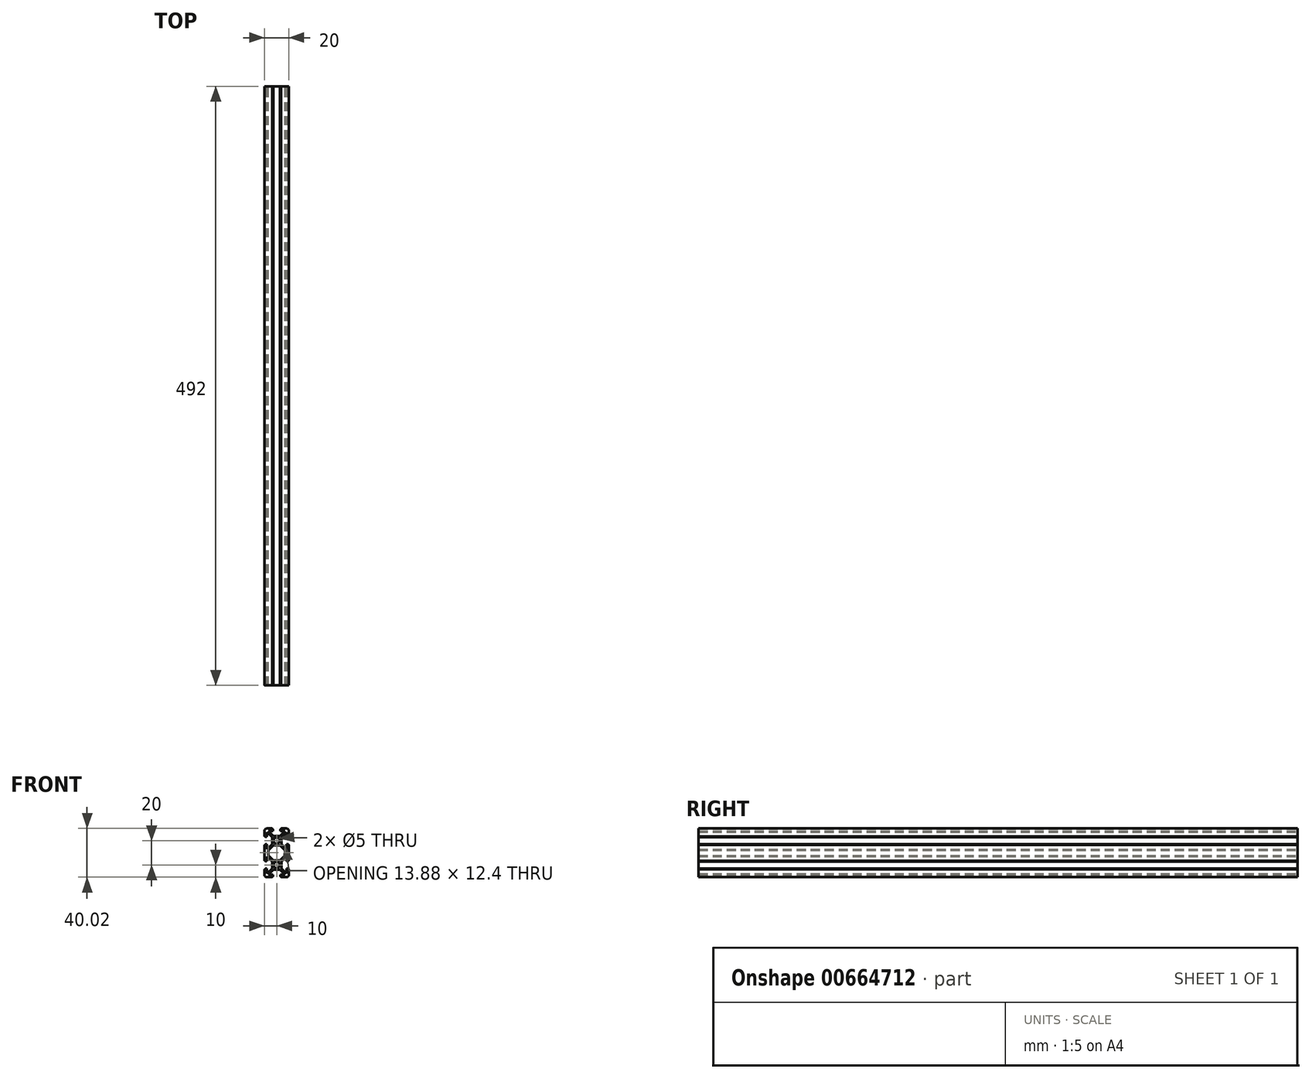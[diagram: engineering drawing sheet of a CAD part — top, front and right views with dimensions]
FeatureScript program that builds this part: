
annotation { "Feature Type Name" : "Feature", "Feature Type Description" : "" }
export const myFeature = defineFeature(function(context is Context, id is Id, definition is map)
    precondition{}
    {
        {
            var Q0;
            Q0=qCreatedBy(makeId("Front.planeOp"),FACE);
            var sketch = newSketch(context, id + "F0", { "sketchPlane" : qUnion([Q0])});
            skPoint(sketch, "E0.middle", {"position": v(10, -10) * mm});
            skPoint(sketch, "E1.visualSharp", {"position": v(0, 0) * mm});
            skArc(sketch, "E1.filletArc", {"start": v(2, 0) * mm, "mid": v(0.59, -0.59) * mm, "end": v(0, -2) * mm});
            skPoint(sketch, "E2.visualSharp", {"position": v(20, 0) * mm});
            skArc(sketch, "E2.filletArc", {"start": v(20, -2) * mm, "mid": v(19.41, -0.59) * mm, "end": v(18, 0) * mm});
            skPoint(sketch, "E3.visualSharp", {"position": v(20, -20) * mm});
            skLineSegment(sketch, "E4", {"start": v(2, 0) * mm, "end": v(6.5, 0) * mm});
            skLineSegment(sketch, "E5", {"start": v(6.5, 0) * mm, "end": v(6.5, -0.5) * mm});
            skLineSegment(sketch, "E6", {"start": v(13.02, -0.5) * mm, "end": v(13.5, -0.5) * mm});
            skLineSegment(sketch, "E7", {"start": v(13.5, 0.02) * mm, "end": v(18, 0) * mm});
            skLineSegment(sketch, "E8", {"start": v(20, -2) * mm, "end": v(20, -6.5) * mm});
            skLineSegment(sketch, "E9", {"start": v(20, -6.5) * mm, "end": v(19.5, -6.5) * mm});
            skLineSegment(sketch, "E10", {"start": v(19.5, -6.5) * mm, "end": v(19.5, -7) * mm});
            skLineSegment(sketch, "E11", {"start": v(13.83, -7.25) * mm, "end": v(13.83, -12.77) * mm});
            skLineSegment(sketch, "E12", {"start": v(19.53, -12.98) * mm, "end": v(19.54, -13.46) * mm});
            skLineSegment(sketch, "E13", {"start": v(12.74, -13.8) * mm, "end": v(7.26, -13.8) * mm});
            skLineSegment(sketch, "E14", {"start": v(6.2, -12.74) * mm, "end": v(6.2, -7.26) * mm});
            skLineSegment(sketch, "E15", {"start": v(0, -6.49) * mm, "end": v(0, -2) * mm});
            skLineSegment(sketch, "E16", {"start": v(7, -0.5) * mm, "end": v(7, -2) * mm});
            skLineSegment(sketch, "E17", {"start": v(7, -2) * mm, "end": v(3.06, -2) * mm});
            skLineSegment(sketch, "E18", {"start": v(3.06, -2) * mm, "end": v(7.26, -6.2) * mm});
            skLineSegment(sketch, "E19", {"start": v(12.74, -6.2) * mm, "end": v(16.94, -2) * mm});
            skLineSegment(sketch, "E20", {"start": v(16.94, -2) * mm, "end": v(13.02, -2) * mm});
            skLineSegment(sketch, "E21", {"start": v(19.53, -12.98) * mm, "end": v(18, -12.98) * mm});
            skLineSegment(sketch, "E22", {"start": v(18, -12.98) * mm, "end": v(18, -16.94) * mm});
            skLineSegment(sketch, "E23", {"start": v(18, -16.94) * mm, "end": v(13.83, -12.77) * mm});
            skLineSegment(sketch, "E24", {"start": v(13.83, -7.25) * mm, "end": v(18, -3.06) * mm});
            skLineSegment(sketch, "E25", {"start": v(18, -3.06) * mm, "end": v(18, -7) * mm});
            skLineSegment(sketch, "E26", {"start": v(18, -7) * mm, "end": v(19.5, -7) * mm});
            skLineSegment(sketch, "E27", {"start": v(16.94, -18) * mm, "end": v(12.74, -13.8) * mm});
            skLineSegment(sketch, "E28", {"start": v(7.26, -13.8) * mm, "end": v(3.06, -18) * mm});
            skLineSegment(sketch, "E29", {"start": v(0.5, -6.49) * mm, "end": v(0.5, -7) * mm});
            skLineSegment(sketch, "E30", {"start": v(0.5, -7) * mm, "end": v(2, -7) * mm});
            skLineSegment(sketch, "E31", {"start": v(2, -7) * mm, "end": v(2, -3.08) * mm});
            skLineSegment(sketch, "E32", {"start": v(2, -3.08) * mm, "end": v(6.2, -7.26) * mm});
            skLineSegment(sketch, "E33", {"start": v(6.2, -12.74) * mm, "end": v(2, -16.94) * mm});
            skLineSegment(sketch, "E34", {"start": v(2, -16.94) * mm, "end": v(2, -13) * mm});
            skLineSegment(sketch, "E35", {"start": v(2, -13) * mm, "end": v(0.5, -13) * mm});
            skLineSegment(sketch, "E36", {"start": v(0.5, -13) * mm, "end": v(0.5, -13.5) * mm});
            skLineSegment(sketch, "E37", {"start": v(0.5, -13.5) * mm, "end": v(0, -13.5) * mm});
            skCircle(sketch, "E38", {"center": v(10, -10) * mm, "radius": 2.5 * mm});
            skLineSegment(sketch, "E39", {"start": v(13.5, 0.02) * mm, "end": v(13.5, -0.5) * mm});
            skLineSegment(sketch, "E40", {"start": v(6.5, -0.5) * mm, "end": v(7, -0.5) * mm});
            skLineSegment(sketch, "E41", {"start": v(13.02, -0.5) * mm, "end": v(13.02, -2) * mm});
            skLineSegment(sketch, "E42", {"start": v(7.26, -6.2) * mm, "end": v(12.74, -6.2) * mm});
            skLineSegment(sketch, "E43", {"start": v(0, -6.49) * mm, "end": v(0.5, -6.49) * mm});
            skLineSegment(sketch, "E44", {"start": v(19.54, -13.46) * mm, "end": v(20, -13.46) * mm});
            skPoint(sketch, "E45.middle", {"position": v(10, -30) * mm});
            skPoint(sketch, "E46.visualSharp", {"position": v(0, -20) * mm});
            skPoint(sketch, "E47.visualSharp", {"position": v(20, -40) * mm});
            skArc(sketch, "E47.filletArc", {"start": v(18, -40) * mm, "mid": v(19.41, -39.41) * mm, "end": v(20, -38) * mm});
            skArc(sketch, "E48.filletArc", {"start": v(0, -38) * mm, "mid": v(0.59, -39.41) * mm, "end": v(2, -40) * mm});
            skLineSegment(sketch, "E49", {"start": v(20, -26.5) * mm, "end": v(19.5, -26.5) * mm});
            skLineSegment(sketch, "E50", {"start": v(19.5, -26.5) * mm, "end": v(19.5, -27) * mm});
            skLineSegment(sketch, "E51", {"start": v(13.83, -27.25) * mm, "end": v(13.83, -32.77) * mm});
            skLineSegment(sketch, "E52", {"start": v(19.53, -32.98) * mm, "end": v(19.54, -33.46) * mm});
            skLineSegment(sketch, "E53", {"start": v(20, -33.46) * mm, "end": v(20, -38) * mm});
            skLineSegment(sketch, "E54", {"start": v(18, -40) * mm, "end": v(13.5, -40) * mm});
            skLineSegment(sketch, "E55", {"start": v(13.5, -40) * mm, "end": v(13.5, -39.5) * mm});
            skLineSegment(sketch, "E56", {"start": v(12.74, -33.8) * mm, "end": v(7.26, -33.8) * mm});
            skLineSegment(sketch, "E57", {"start": v(7, -39.5) * mm, "end": v(6.5, -39.5) * mm});
            skLineSegment(sketch, "E58", {"start": v(6.5, -39.5) * mm, "end": v(6.5, -40) * mm});
            skLineSegment(sketch, "E59", {"start": v(6.5, -40) * mm, "end": v(2, -40) * mm});
            skLineSegment(sketch, "E60", {"start": v(0, -38) * mm, "end": v(0, -33.5) * mm});
            skLineSegment(sketch, "E61", {"start": v(6.2, -32.74) * mm, "end": v(6.2, -27.26) * mm});
            skLineSegment(sketch, "E62", {"start": v(7, -39.5) * mm, "end": v(7, -38) * mm});
            skLineSegment(sketch, "E63", {"start": v(13.02, -39.5) * mm, "end": v(13.02, -38) * mm});
            skLineSegment(sketch, "E64", {"start": v(13.02, -38) * mm, "end": v(16.94, -38) * mm});
            skLineSegment(sketch, "E65", {"start": v(3.06, -22) * mm, "end": v(7.26, -26.2) * mm});
            skLineSegment(sketch, "E66", {"start": v(12.74, -26.2) * mm, "end": v(16.94, -22) * mm});
            skLineSegment(sketch, "E67", {"start": v(19.53, -32.98) * mm, "end": v(18, -32.98) * mm});
            skLineSegment(sketch, "E68", {"start": v(18, -32.98) * mm, "end": v(18, -36.94) * mm});
            skLineSegment(sketch, "E69", {"start": v(18, -36.94) * mm, "end": v(13.83, -32.77) * mm});
            skLineSegment(sketch, "E70", {"start": v(13.83, -27.25) * mm, "end": v(18, -23.06) * mm});
            skLineSegment(sketch, "E71", {"start": v(18, -23.06) * mm, "end": v(18, -27) * mm});
            skLineSegment(sketch, "E72", {"start": v(18, -27) * mm, "end": v(19.5, -27) * mm});
            skLineSegment(sketch, "E73", {"start": v(13.5, -39.5) * mm, "end": v(13.02, -39.5) * mm});
            skLineSegment(sketch, "E74", {"start": v(16.94, -38) * mm, "end": v(12.74, -33.8) * mm});
            skLineSegment(sketch, "E75", {"start": v(7.26, -33.8) * mm, "end": v(3.06, -38) * mm});
            skLineSegment(sketch, "E76", {"start": v(3.06, -38) * mm, "end": v(7, -38) * mm});
            skLineSegment(sketch, "E77", {"start": v(7, -38) * mm, "end": v(7, -39.5) * mm});
            skLineSegment(sketch, "E78", {"start": v(0.5, -26.49) * mm, "end": v(0.5, -27) * mm});
            skLineSegment(sketch, "E79", {"start": v(0.5, -27) * mm, "end": v(2, -27) * mm});
            skLineSegment(sketch, "E80", {"start": v(2, -27) * mm, "end": v(2, -23.08) * mm});
            skLineSegment(sketch, "E81", {"start": v(2, -23.08) * mm, "end": v(6.2, -27.26) * mm});
            skLineSegment(sketch, "E82", {"start": v(6.2, -32.74) * mm, "end": v(2, -36.94) * mm});
            skLineSegment(sketch, "E83", {"start": v(2, -36.94) * mm, "end": v(2, -33) * mm});
            skLineSegment(sketch, "E84", {"start": v(2, -33) * mm, "end": v(0.5, -33) * mm});
            skLineSegment(sketch, "E85", {"start": v(0.5, -33) * mm, "end": v(0.5, -33.5) * mm});
            skLineSegment(sketch, "E86", {"start": v(0.5, -33.5) * mm, "end": v(0, -33.5) * mm});
            skCircle(sketch, "E87", {"center": v(10, -30) * mm, "radius": 2.5 * mm});
            skLineSegment(sketch, "E88", {"start": v(7.26, -26.2) * mm, "end": v(12.74, -26.2) * mm});
            skLineSegment(sketch, "E89", {"start": v(0, -26.49) * mm, "end": v(0.5, -26.49) * mm});
            skLineSegment(sketch, "E90", {"start": v(19.54, -33.46) * mm, "end": v(20, -33.46) * mm});
            skLineSegment(sketch, "E91", {"start": v(0, -13.5) * mm, "end": v(0, -26.49) * mm});
            skLineSegment(sketch, "E92", {"start": v(3.06, -18) * mm, "end": v(3.06, -22) * mm});
            skLineSegment(sketch, "E93", {"start": v(16.94, -18) * mm, "end": v(16.94, -22) * mm});
            skLineSegment(sketch, "E94", {"start": v(20, -13.46) * mm, "end": v(20, -26.5) * mm});
            skSolve(sketch);
        }
        {
            assignVariable(context, id + "F1", {"name" : "L", "anyValue" : 492 * mm});
        }
        {
            var Q0;
            Q0=makeQuery(id+"F0.imprint","IMPRINT",FACE,{"disambiguationData":[TD([[makeQuery(id+"F0.imprint","IMPRINT",EDGE,{"derivedFrom":sQuery(id+"F0.wireOp",EDGE,"E1.filletArc")}),1.0]])]});
            extrude(context, id + "F2", {"entities" : qUnion([Q0]), "depth" : getVariable(context, 'L'), "offsetDistance" : 25 * mm});
        }
    });
